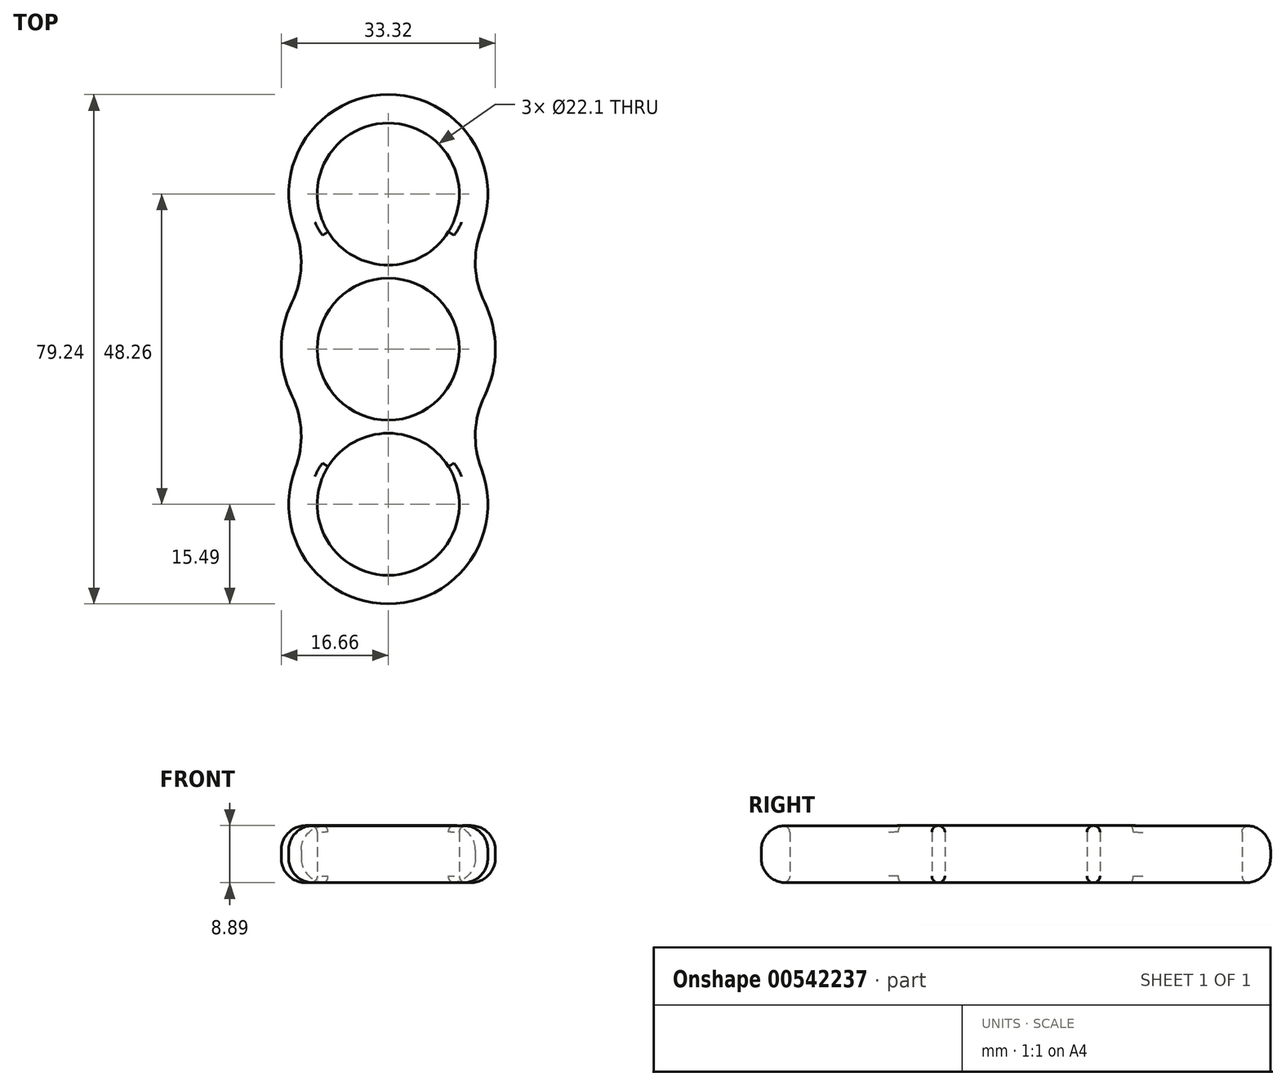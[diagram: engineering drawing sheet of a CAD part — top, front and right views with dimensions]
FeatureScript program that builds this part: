
annotation { "Feature Type Name" : "Feature", "Feature Type Description" : "" }
export const myFeature = defineFeature(function(context is Context, id is Id, definition is map)
    precondition{}
    {
        {
            var Q0;
            Q0=qCreatedBy(makeId("Top.planeOp"),FACE);
            var sketch = newSketch(context, id + "F0", { "sketchPlane" : qUnion([Q0])});
            skCircle(sketch, "E0", {"center": v(0, 0) * mm, "radius": 11.05 * mm});
            skCircle(sketch, "E1.1.0", {"center": v(0, -24.13) * mm, "radius": 11.05 * mm});
            skArc(sketch, "E2.1.1", {"start": v(-9.58, -18.6) * mm, "mid": v(0, -35.19) * mm, "end": v(9.58, -18.6) * mm});
            skArc(sketch, "E3", {"start": v(-14.48, -18.61) * mm, "mid": v(0, -39.62) * mm, "end": v(14.48, -18.61) * mm});
            skArc(sketch, "E4", {"start": v(-14.98, 7.28) * mm, "mid": v(-16.66, 0) * mm, "end": v(-14.98, -7.28) * mm});
            skArc(sketch, "E5", {"start": v(14.48, 18.61) * mm, "mid": v(13.56, 12.9) * mm, "end": v(14.98, 7.28) * mm});
            skCircle(sketch, "E6", {"center": v(0, 24.13) * mm, "radius": 11.05 * mm});
            skArc(sketch, "E7", {"start": v(14.48, 18.61) * mm, "mid": v(0, 39.62) * mm, "end": v(-14.48, 18.61) * mm});
            skArc(sketch, "E8.MirrorCS", {"start": v(-14.48, 18.61) * mm, "mid": v(-13.56, 12.9) * mm, "end": v(-14.98, 7.28) * mm});
            skArc(sketch, "E9.MirrorCS", {"start": v(-14.48, -18.61) * mm, "mid": v(-13.56, -12.9) * mm, "end": v(-14.98, -7.28) * mm});
            skArc(sketch, "E10.MirrorCS", {"start": v(14.48, -18.61) * mm, "mid": v(13.56, -12.9) * mm, "end": v(14.98, -7.28) * mm});
            skArc(sketch, "E11.trimOffspring", {"start": v(14.98, -7.28) * mm, "mid": v(16.66, 0) * mm, "end": v(14.98, 7.28) * mm});
            skSolve(sketch);
        }
        {
            var Q0;
            Q0=makeQuery(id+"F0.imprint","IMPRINT",FACE,{"disambiguationData":[TD([[makeQuery(id+"F0.imprint","IMPRINT",EDGE,{"derivedFrom":sQuery(id+"F0.wireOp",EDGE,"E0")}),-1.0]])]});
            extrude(context, id + "F1", {"entities" : qUnion([Q0]), "depth" : 8.9 * mm, "offsetDistance" : 25.4 * mm});
        }
        {
            var Q0;
            Q0=makeQuery(id+"F1.opExtrude","CAP_EDGE",EDGE,{"disambiguationData":[OSD([sQuery(id+"F0.wireOp",EDGE,"E10.MirrorCS")])],"isStart":true});
            var Q1;
            Q1=makeQuery(id+"F1.opExtrude","CAP_EDGE",EDGE,{"disambiguationData":[OSD([sQuery(id+"F0.wireOp",EDGE,"E3")])],"isStart":false});
            fillet(context, id + "F2", {"entities" : qUnion([Q0, Q1]), "radius" : 3.8 * mm, "tangentPropagation" : true, "allowEdgeOverflow" : false});
        }
        {
            var Q0;
            Q0=makeQuery(id+"F1.opExtrude","CAP_EDGE",EDGE,{"disambiguationData":[OSD([sQuery(id+"F0.wireOp",EDGE,"E1.1.0")])],"isStart":false});
            var Q1;
            Q1=makeQuery(id+"F1.opExtrude","CAP_EDGE",EDGE,{"disambiguationData":[OSD([sQuery(id+"F0.wireOp",EDGE,"E0")])],"isStart":false});
            var Q2;
            Q2=makeQuery(id+"F1.opExtrude","CAP_EDGE",EDGE,{"disambiguationData":[OSD([sQuery(id+"F0.wireOp",EDGE,"E6")])],"isStart":false});
            var Q3;
            Q3=makeQuery(id+"F1.opExtrude","CAP_EDGE",EDGE,{"disambiguationData":[OSD([sQuery(id+"F0.wireOp",EDGE,"E6")])],"isStart":true});
            var Q4;
            Q4=makeQuery(id+"F1.opExtrude","CAP_EDGE",EDGE,{"disambiguationData":[OSD([sQuery(id+"F0.wireOp",EDGE,"E0")])],"isStart":true});
            var Q5;
            Q5=makeQuery(id+"F1.opExtrude","CAP_EDGE",EDGE,{"disambiguationData":[OSD([sQuery(id+"F0.wireOp",EDGE,"E1.1.0")])],"isStart":true});
            fillet(context, id + "F3", {"entities" : qUnion([Q0, Q1, Q2, Q3, Q4, Q5]), "radius" : 1.02 * mm, "tangentPropagation" : true, "allowEdgeOverflow" : false});
        }
    });
